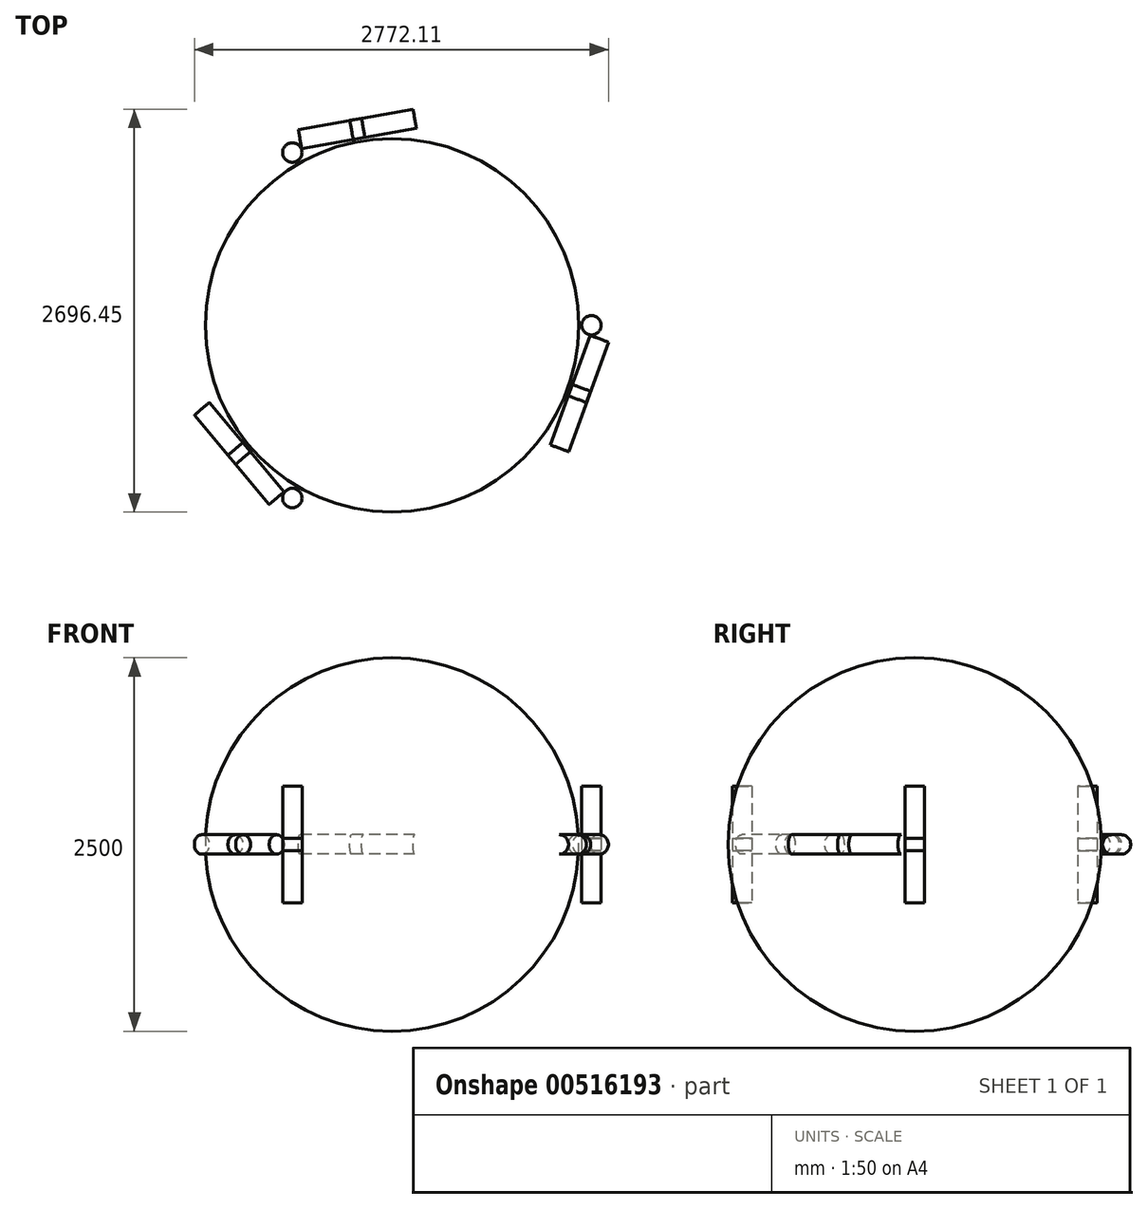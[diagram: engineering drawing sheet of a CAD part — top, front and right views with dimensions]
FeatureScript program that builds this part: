
annotation { "Feature Type Name" : "Feature", "Feature Type Description" : "" }
export const myFeature = defineFeature(function(context is Context, id is Id, definition is map)
    precondition{}
    {
        {
            var Q0;
            Q0=qCreatedBy(makeId("Front.planeOp"),FACE);
            var sketch = newSketch(context, id + "F0", { "sketchPlane" : qUnion([Q0])});
            skArc(sketch, "E0", {"start": v(0, -1250) * mm, "mid": v(1250, 0) * mm, "end": v(0, 1250) * mm});
            skLineSegment(sketch, "E1", {"start": v(0, 1250) * mm, "end": v(0, -1250) * mm});
            skSolve(sketch);
        }
        {
            var Q0;
            Q0=makeQuery(id+"F0.imprint","IMPRINT",FACE,{"disambiguationData":[TD([[makeQuery(id+"F0.imprint","IMPRINT",EDGE,{"derivedFrom":sQuery(id+"F0.wireOp",EDGE,"E0")}),1.0]])]});
            var Q1;
            Q1=sQuery(id+"F0.wireOp",EDGE,"E1");
            revolve(context, id + "F1", {"entities" : qUnion([Q0]), "axis" : qUnion([Q1]), "revolveType" : RevolveType.FULL});
        }
        {
            var Q0;
            Q0=qCreatedBy(makeId("Front.planeOp"),FACE);
            var sketch = newSketch(context, id + "F2", { "sketchPlane" : qUnion([Q0])});
            skCircle(sketch, "E2", {"center": v(1335, 0) * mm, "radius": 65 * mm});
            skLineSegment(sketch, "E3", {"start": v(1335, 0) * mm, "end": v(0, 0) * mm, "construction": true});
            skCircle(sketch, "E4", {"center": v(0, 0) * mm, "radius": 1250 * mm});
            skSolve(sketch);
        }
        {
            var Q0;
            Q0=makeQuery(id+"F2.imprint","IMPRINT",FACE,{"disambiguationData":[TD([[makeQuery(id+"F2.imprint","IMPRINT",EDGE,{"derivedFrom":sQuery(id+"F2.wireOp",EDGE,"E2")}),1.0]])]});
            extrude(context, id + "F3", {"entities" : qUnion([Q0]), "endBound" : BoundingType.SYMMETRIC, "depth" : 80 * mm, "offsetDistance" : 25 * mm});
        }
        {
            var Q0;
            Q0=makeQuery(id+"F2.imprint","IMPRINT",FACE,{"disambiguationData":[TD([[makeQuery(id+"F2.imprint","IMPRINT",EDGE,{"derivedFrom":sQuery(id+"F2.wireOp",EDGE,"E2")}),1.0]])]});
            extrude(context, id + "F4", {"entities" : qUnion([Q0]), "endBound" : BoundingType.SYMMETRIC, "depth" : (6 * 130) * mm, "offsetDistance" : 25 * mm});
        }
        {
            var Q0;
            Q0=makeQuery(id+"F3.opExtrude","SWEPT_BODY",BODY,{"disambiguationData":[OSD([sQuery(id+"F2.wireOp",EDGE,"E2")])]});
            var Q1;
            Q1=makeQuery(id+"F4.opExtrude","SWEPT_BODY",BODY,{"disambiguationData":[OSD([sQuery(id+"F2.wireOp",EDGE,"E2")])]});
            var Q2;
            Q2=sQuery(id+"F0.wireOp",EDGE,"E1");
            circularPattern(context, id + "F5", {"entities" : qUnion([Q0, Q1]), "axis" : qUnion([Q2]), "angle" : 20 * degree, "instanceCount" : 2, "equalSpace" : true});
        }
        {
            var Q0;
            Q0=makeQuery(id+"F3.opExtrude","SWEPT_BODY",BODY,{"disambiguationData":[OSD([sQuery(id+"F2.wireOp",EDGE,"E2")])]});
            var Q1;
            Q1=makeQuery(id+"F4.opExtrude","SWEPT_BODY",BODY,{"disambiguationData":[OSD([sQuery(id+"F2.wireOp",EDGE,"E2")])]});
            var Q2;
            Q2=sQuery(id+"F2.wireOp",EDGE,"E3");
            transform(context, id + "F6", {"entities" : qUnion([Q0, Q1]), "transformType" : TransformType.ROTATION, "transformAxis" : qUnion([Q2]), "angle" : 90 * degree, "makeCopy" : false});
        }
        {
            var Q0;
            Q0=makeQuery(id+"F4.opExtrude","SWEPT_BODY",BODY,{"disambiguationData":[OSD([sQuery(id+"F2.wireOp",EDGE,"E2")])]});
            var Q1;
            Q1=makeQuery(id+"F3.opExtrude","SWEPT_BODY",BODY,{"disambiguationData":[OSD([sQuery(id+"F2.wireOp",EDGE,"E2")])]});
            var Q2;
            Q2=makeQuery(id+"F5.opPattern","COPY",BODY,{"derivedFrom":makeQuery(id+"F4.opExtrude","SWEPT_BODY",BODY,{"disambiguationData":[OSD([sQuery(id+"F2.wireOp",EDGE,"E2")])]}),"instanceName":"1"});
            var Q3;
            Q3=makeQuery(id+"F5.opPattern","COPY",BODY,{"derivedFrom":makeQuery(id+"F3.opExtrude","SWEPT_BODY",BODY,{"disambiguationData":[OSD([sQuery(id+"F2.wireOp",EDGE,"E2")])]}),"instanceName":"1"});
            var Q4;
            Q4=sQuery(id+"F0.wireOp",EDGE,"E1");
            circularPattern(context, id + "F7", {"entities" : qUnion([Q0, Q1, Q2, Q3]), "axis" : qUnion([Q4]), "angle" : 360 * degree, "instanceCount" : 3, "equalSpace" : true});
        }
    });
